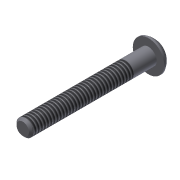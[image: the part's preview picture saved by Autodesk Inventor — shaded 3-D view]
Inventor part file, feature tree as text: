
AUTODESK INVENTOR PART (.ipt)
format: ipt  version: 2013 (Build 170138000, 138)  size: 111,616 bytes
history: native  units: in
note: dims shown in document units (in); Inventor stores cm internally (conversion verified against a paired STEP export)
features: sketch x3, extrude x2, revolve x1, chamfer x1, thread x1
ambient origin geometry x8: Origin, YZ Plane, XZ Plane, XY Plane, X Axis, Y Axis, Z Axis, Center Point
bodies: Solid1 (feature_tree)
feature tree (8):
  extrude  "Extrusion1"  Depth=1.25in TaperAngle=0.0deg
  revolve  "Revolution1"  [1 undecoded]
  extrude  "Extrusion2"  Depth=0.0938in
  chamfer  "Chamfer1"  Distance=0.0625in
  thread  "Thread1"  [1 undecoded]
  sketch  "Sketch1"  dims[d0=0.164in d1=1.25in d2=0.0in]
  sketch  "Sketch2"  dims[d3=0.087in d6=0.08in]
  sketch  "Sketch3"  dims[d7=90.0deg d8=0.0938in d9=0.0625in d10=0.0in d13=0.02in d14=0.125in d15=45.0deg d16=1.0in d17=0.0in d19=0.156in]
note: 2 required parameter values undecoded (feature->parameter linkage not recoverable at this tier; creation-order binding heuristic only, values carry confidence <= 0.55)